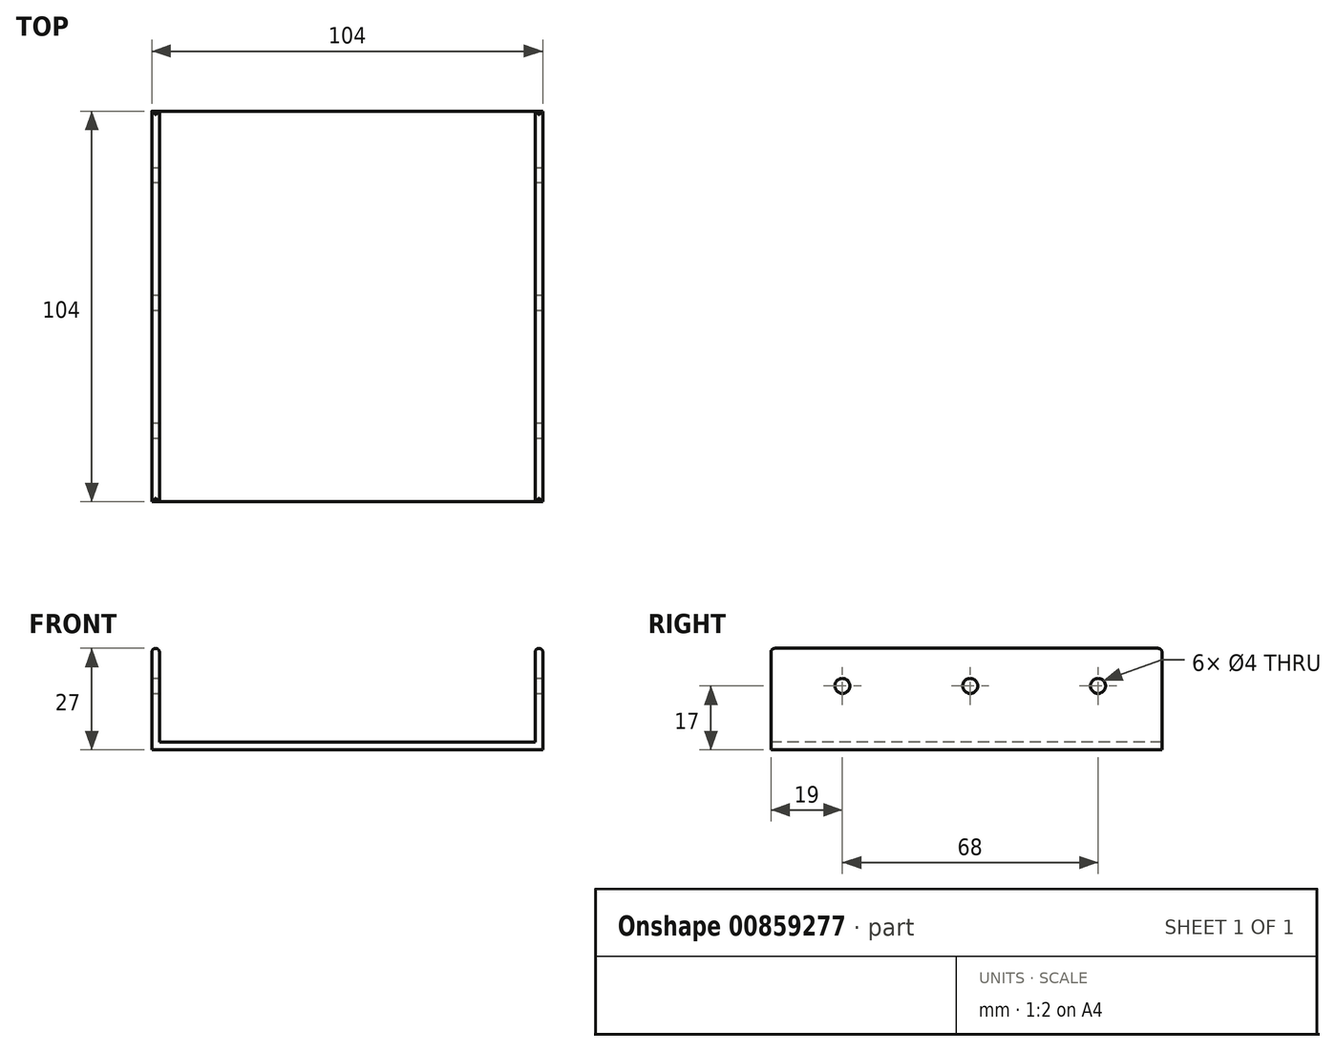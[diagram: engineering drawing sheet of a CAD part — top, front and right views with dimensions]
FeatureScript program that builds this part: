
annotation { "Feature Type Name" : "Feature", "Feature Type Description" : "" }
export const myFeature = defineFeature(function(context is Context, id is Id, definition is map)
    precondition{}
    {
        {
            var Q0;
            Q0=qCreatedBy(makeId("Top.planeOp"),FACE);
            var sketch = newSketch(context, id + "F0", { "sketchPlane" : qUnion([Q0])});
            skLineSegment(sketch, "E0.bottom", {"start": v(-52, 52) * mm, "end": v(52, 52) * mm});
            skLineSegment(sketch, "E0.top", {"start": v(-52, -52) * mm, "end": v(52, -52) * mm});
            skLineSegment(sketch, "E0.left", {"start": v(-52, 52) * mm, "end": v(-52, -52) * mm});
            skLineSegment(sketch, "E0.right", {"start": v(52, 52) * mm, "end": v(52, -52) * mm});
            skPoint(sketch, "E0.middle", {"position": v(0, 0) * mm});
            skSolve(sketch);
        }
        {
            var Q0;
            Q0 = qSketchRegion(id + "F0", true);
            extrude(context, id + "F1", {"entities" : qUnion([Q0]), "depth" : 2 * mm, "offsetDistance" : 25 * mm});
        }
        {
            var Q0;
            Q0=makeQuery(id+"F1.opExtrude","CAP_FACE",FACE,{"disambiguationData":[OSD([sQuery(id+"F0.wireOp",EDGE,"E0.bottom"),sQuery(id+"F0.wireOp",EDGE,"E0.top"),sQuery(id+"F0.wireOp",EDGE,"E0.left"),sQuery(id+"F0.wireOp",EDGE,"E0.right")])],"isStart":false});
            var sketch = newSketch(context, id + "F2", { "sketchPlane" : qUnion([Q0])});
            skLineSegment(sketch, "E1.bottom", {"start": v(-52, 52) * mm, "end": v(-50, 52) * mm});
            skLineSegment(sketch, "E1.top", {"start": v(-52, -52) * mm, "end": v(-50, -52) * mm});
            skLineSegment(sketch, "E1.left", {"start": v(-52, 52) * mm, "end": v(-52, -52) * mm});
            skLineSegment(sketch, "E1.right", {"start": v(-50, 52) * mm, "end": v(-50, -52) * mm});
            skSolve(sketch);
        }
        {
            var Q0;
            Q0 = qSketchRegion(id + "F2", true);
            extrude(context, id + "F3", {"entities" : qUnion([Q0]), "operationType" : NewBodyOperationType.ADD, "depth" : 25 * mm, "offsetDistance" : 25 * mm});
        }
        {
            var Q0;
            Q0=makeQuery(id+"F1.opExtrude","CAP_FACE",FACE,{"disambiguationData":[OSD([sQuery(id+"F0.wireOp",EDGE,"E0.bottom"),sQuery(id+"F0.wireOp",EDGE,"E0.top"),sQuery(id+"F0.wireOp",EDGE,"E0.left"),sQuery(id+"F0.wireOp",EDGE,"E0.right")])],"isStart":false});
            var sketch = newSketch(context, id + "F4", { "sketchPlane" : qUnion([Q0])});
            skLineSegment(sketch, "E2.bottom", {"start": v(52, 52) * mm, "end": v(50, 52) * mm});
            skLineSegment(sketch, "E2.top", {"start": v(52, -52) * mm, "end": v(50, -52) * mm});
            skLineSegment(sketch, "E2.left", {"start": v(52, 52) * mm, "end": v(52, -52) * mm});
            skLineSegment(sketch, "E2.right", {"start": v(50, 52) * mm, "end": v(50, -52) * mm});
            skSolve(sketch);
        }
        {
            var Q0;
            Q0 = qSketchRegion(id + "F4", true);
            extrude(context, id + "F5", {"entities" : qUnion([Q0]), "operationType" : NewBodyOperationType.ADD, "depth" : 25 * mm, "offsetDistance" : 25 * mm});
        }
        {
            var Q0;
            Q0=makeQuery(id+"F5.opExtrude","CAP_FACE",FACE,{"disambiguationData":[OSD([sQuery(id+"F4.wireOp",EDGE,"E2.bottom"),sQuery(id+"F4.wireOp",EDGE,"E2.top"),sQuery(id+"F4.wireOp",EDGE,"E2.left"),sQuery(id+"F4.wireOp",EDGE,"E2.right")])],"isStart":false});
            fillet(context, id + "F6", {"entities" : qUnion([Q0]), "radius" : 1 * mm, "tangentPropagation" : true, "allowEdgeOverflow" : false});
        }
        {
            var Q0;
            Q0=makeQuery(id+"F3.opExtrude","CAP_FACE",FACE,{"disambiguationData":[OSD([sQuery(id+"F2.wireOp",EDGE,"E1.bottom"),sQuery(id+"F2.wireOp",EDGE,"E1.top"),sQuery(id+"F2.wireOp",EDGE,"E1.left"),sQuery(id+"F2.wireOp",EDGE,"E1.right")])],"isStart":false});
            fillet(context, id + "F7", {"entities" : qUnion([Q0]), "radius" : 1 * mm, "tangentPropagation" : true, "allowEdgeOverflow" : false});
        }
        {
            var Q0;
            Q0=makeQuery(id+"F5.boolean.opBoolean","MERGE",FACE,{"derivedFrom":[makeQuery(id+"F1.opExtrude","SWEPT_FACE",FACE,{"disambiguationData":[OSD([sQuery(id+"F0.wireOp",EDGE,"E0.right")])]}),makeQuery(id+"F5.opExtrude","SWEPT_FACE",FACE,{"disambiguationData":[OSD([sQuery(id+"F4.wireOp",EDGE,"E2.left")])]})]});
            var sketch = newSketch(context, id + "F8", { "sketchPlane" : qUnion([Q0])});
            skCircle(sketch, "E3", {"center": v(-33, 17) * mm, "radius": 2.83 * mm});
            skSolve(sketch);
        }
        {
            var Q0;
            Q0=sQuery(id+"F8.wireOp",VERTEX,"E3.center");
            var Q1;
            Q1=makeQuery(id+"F1.opExtrude","SWEPT_BODY",BODY,{"disambiguationData":[OSD([sQuery(id+"F0.wireOp",EDGE,"E0.bottom"),sQuery(id+"F0.wireOp",EDGE,"E0.top"),sQuery(id+"F0.wireOp",EDGE,"E0.left"),sQuery(id+"F0.wireOp",EDGE,"E0.right")])]});
            hole(context, id + "F9", {"style" : HoleStyle.SIMPLE, "endStyle" : HoleEndStyle.THROUGH, "holeDiameter" : 4 * mm, "majorDiameter" : 5 * mm, "isTappedThrough" : true, "tappedDepth" : 12 * mm, "tapClearance" : 3, "locations" : qUnion([Q0]), "scope" : qUnion([Q1])});
        }
        {
            var Q0;
            Q0=makeQuery(id+"F5.boolean.opBoolean","MERGE",FACE,{"derivedFrom":[makeQuery(id+"F1.opExtrude","SWEPT_FACE",FACE,{"disambiguationData":[OSD([sQuery(id+"F0.wireOp",EDGE,"E0.right")])]}),makeQuery(id+"F5.opExtrude","SWEPT_FACE",FACE,{"disambiguationData":[OSD([sQuery(id+"F4.wireOp",EDGE,"E2.left")])]})]});
            var sketch = newSketch(context, id + "F10", { "sketchPlane" : qUnion([Q0])});
            skCircle(sketch, "E4", {"center": v(1, 17) * mm, "radius": 2 * mm});
            skSolve(sketch);
        }
        {
            var Q0;
            Q0=sQuery(id+"F10.wireOp",VERTEX,"E4.center");
            var Q1;
            Q1=makeQuery(id+"F1.opExtrude","SWEPT_BODY",BODY,{"disambiguationData":[OSD([sQuery(id+"F0.wireOp",EDGE,"E0.bottom"),sQuery(id+"F0.wireOp",EDGE,"E0.top"),sQuery(id+"F0.wireOp",EDGE,"E0.left"),sQuery(id+"F0.wireOp",EDGE,"E0.right")])]});
            hole(context, id + "F11", {"style" : HoleStyle.SIMPLE, "endStyle" : HoleEndStyle.THROUGH, "holeDiameter" : 4 * mm, "majorDiameter" : 5 * mm, "isTappedThrough" : true, "tappedDepth" : 12 * mm, "tapClearance" : 3, "locations" : qUnion([Q0]), "scope" : qUnion([Q1])});
        }
        {
            var Q0;
            Q0=makeQuery(id+"F5.boolean.opBoolean","MERGE",FACE,{"derivedFrom":[makeQuery(id+"F1.opExtrude","SWEPT_FACE",FACE,{"disambiguationData":[OSD([sQuery(id+"F0.wireOp",EDGE,"E0.right")])]}),makeQuery(id+"F5.opExtrude","SWEPT_FACE",FACE,{"disambiguationData":[OSD([sQuery(id+"F4.wireOp",EDGE,"E2.left")])]})]});
            var sketch = newSketch(context, id + "F12", { "sketchPlane" : qUnion([Q0])});
            skCircle(sketch, "E5", {"center": v(35, 17) * mm, "radius": 2 * mm});
            skSolve(sketch);
        }
        {
            var Q0;
            Q0=sQuery(id+"F12.wireOp",VERTEX,"E5.center");
            var Q1;
            Q1=makeQuery(id+"F1.opExtrude","SWEPT_BODY",BODY,{"disambiguationData":[OSD([sQuery(id+"F0.wireOp",EDGE,"E0.bottom"),sQuery(id+"F0.wireOp",EDGE,"E0.top"),sQuery(id+"F0.wireOp",EDGE,"E0.left"),sQuery(id+"F0.wireOp",EDGE,"E0.right")])]});
            hole(context, id + "F13", {"style" : HoleStyle.SIMPLE, "endStyle" : HoleEndStyle.THROUGH, "holeDiameter" : 4 * mm, "majorDiameter" : 5 * mm, "isTappedThrough" : true, "tappedDepth" : 12 * mm, "tapClearance" : 3, "locations" : qUnion([Q0]), "scope" : qUnion([Q1])});
        }
    });
